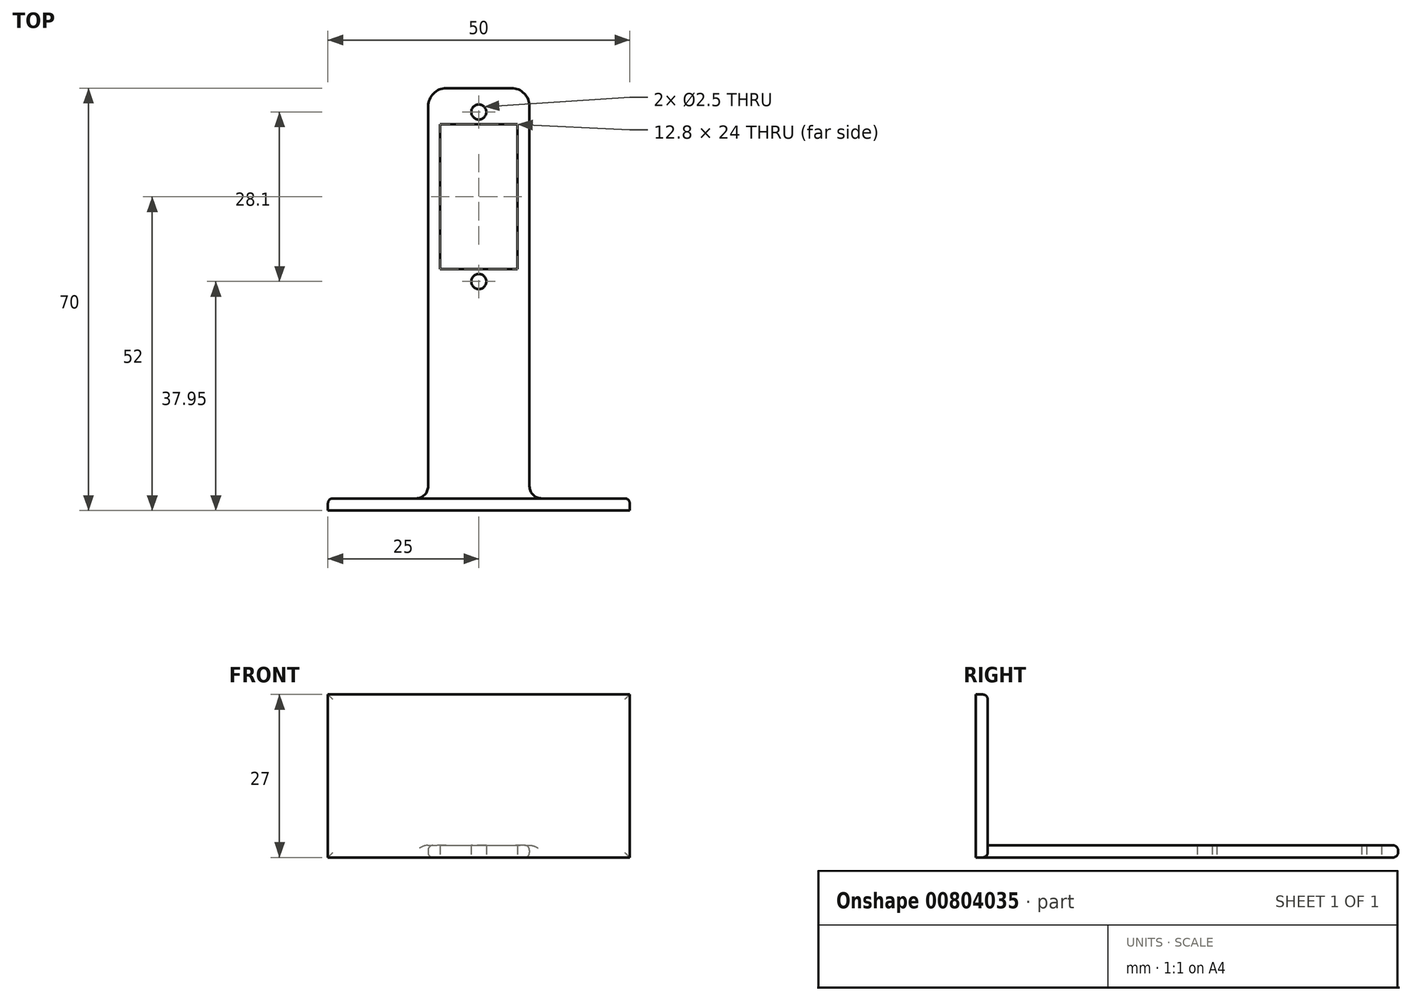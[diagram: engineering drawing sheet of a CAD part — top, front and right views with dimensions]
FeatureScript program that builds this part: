
annotation { "Feature Type Name" : "Feature", "Feature Type Description" : "" }
export const myFeature = defineFeature(function(context is Context, id is Id, definition is map)
    precondition{}
    {
        {
            assignVariable(context, id + "F0", {"name" : "wallT", "anyValue" : 2});
        }
        {
            var Q0;
            Q0=qCreatedBy(makeId("Top.planeOp"),FACE);
            var sketch = newSketch(context, id + "F1", { "sketchPlane" : qUnion([Q0])});
            skLineSegment(sketch, "E0.bottom", {"start": v(-5.4, 35) * mm, "end": v(5.4, 35) * mm});
            skLineSegment(sketch, "E0.top", {"start": v(-8.4, -35) * mm, "end": v(8.4, -35) * mm});
            skLineSegment(sketch, "E0.left", {"start": v(-8.4, 32) * mm, "end": v(-8.4, -35) * mm});
            skLineSegment(sketch, "E0.right", {"start": v(8.4, 32) * mm, "end": v(8.4, -35) * mm});
            skLineSegment(sketch, "E1", {"start": v(-6.63, 0) * mm, "end": v(6.86, 0) * mm, "construction": true});
            skLineSegment(sketch, "E2", {"start": v(0, 7.52) * mm, "end": v(0, -9.29) * mm, "construction": true});
            skLineSegment(sketch, "E3.bottom", {"start": v(-6.4, 29) * mm, "end": v(6.4, 29) * mm});
            skLineSegment(sketch, "E3.top", {"start": v(-6.4, 5) * mm, "end": v(6.4, 5) * mm});
            skLineSegment(sketch, "E3.left", {"start": v(-6.4, 29) * mm, "end": v(-6.4, 5) * mm});
            skLineSegment(sketch, "E3.right", {"start": v(6.4, 29) * mm, "end": v(6.4, 5) * mm});
            skCircle(sketch, "E4", {"center": v(0, 31.05) * mm, "radius": 1.25 * mm});
            skCircle(sketch, "E5", {"center": v(0, 2.95) * mm, "radius": 1.25 * mm});
            skLineSegment(sketch, "E6", {"start": v(-7.84, 17) * mm, "end": v(7.5, 17) * mm, "construction": true});
            skPoint(sketch, "E6.startSnap0", {"position": v(-6.4, 17) * mm});
            skPoint(sketch, "E7.visualSharp", {"position": v(-8.4, 35) * mm});
            skArc(sketch, "E7.filletArc", {"start": v(-5.4, 35) * mm, "mid": v(-7.52, 34.12) * mm, "end": v(-8.4, 32) * mm});
            skPoint(sketch, "E8.visualSharp", {"position": v(8.4, 35) * mm});
            skArc(sketch, "E8.filletArc", {"start": v(8.4, 32) * mm, "mid": v(7.52, 34.12) * mm, "end": v(5.4, 35) * mm});
            skSolve(sketch);
        }
        {
            var Q0;
            Q0 = qSketchRegion(id + "F1", true);
            extrude(context, id + "F2", {"entities" : qUnion([Q0]), "depth" : (getVariable(context, 'wallT')) * mm, "offsetDistance" : 25 * mm});
        }
        {
            var Q0;
            Q0=makeQuery(id+"F2.opExtrude","CAP_FACE",FACE,{"disambiguationData":[OSD([sQuery(id+"F1.wireOp",EDGE,"E0.bottom"),sQuery(id+"F1.wireOp",EDGE,"E0.top"),sQuery(id+"F1.wireOp",EDGE,"E0.left"),sQuery(id+"F1.wireOp",EDGE,"E0.right")])],"isStart":false});
            var sketch = newSketch(context, id + "F3", { "sketchPlane" : qUnion([Q0])});
            skLineSegment(sketch, "E9.bottom", {"start": v(-8.4, -35) * mm, "end": v(8.4, -35) * mm});
            skLineSegment(sketch, "E9.top", {"start": v(-8.4, -33) * mm, "end": v(8.4, -33) * mm});
            skLineSegment(sketch, "E9.left", {"start": v(-8.4, -35) * mm, "end": v(-8.4, -33) * mm});
            skLineSegment(sketch, "E9.right", {"start": v(8.4, -35) * mm, "end": v(8.4, -33) * mm});
            skSolve(sketch);
        }
        {
            var Q0;
            Q0 = qSketchRegion(id + "F3", true);
            extrude(context, id + "F4", {"entities" : qUnion([Q0]), "operationType" : NewBodyOperationType.ADD, "depth" : 25 * mm, "offsetDistance" : 25 * mm});
        }
        {
            var Q0;
            Q0=makeQuery(id+"F4.boolean.opBoolean","MERGE",FACE,{"derivedFrom":[makeQuery(id+"F2.opExtrude","SWEPT_FACE",FACE,{"disambiguationData":[OSD([sQuery(id+"F1.wireOp",EDGE,"E0.top")])]}),makeQuery(id+"F4.opExtrude","SWEPT_FACE",FACE,{"disambiguationData":[OSD([sQuery(id+"F3.wireOp",EDGE,"E9.bottom")])]})]});
            var sketch = newSketch(context, id + "F5", { "sketchPlane" : qUnion([Q0])});
            skLineSegment(sketch, "E10.bottom", {"start": v(-25, 27) * mm, "end": v(25, 27) * mm});
            skLineSegment(sketch, "E10.top", {"start": v(-25, 0) * mm, "end": v(25, 0) * mm});
            skLineSegment(sketch, "E10.left", {"start": v(-25, 27) * mm, "end": v(-25, 0) * mm});
            skLineSegment(sketch, "E10.right", {"start": v(25, 27) * mm, "end": v(25, 0) * mm});
            skLineSegment(sketch, "E11", {"start": v(0, -3.84) * mm, "end": v(0, 7.26) * mm, "construction": true});
            skSolve(sketch);
        }
        {
            var Q0;
            Q0 = qSketchRegion(id + "F5", true);
            extrude(context, id + "F6", {"entities" : qUnion([Q0]), "operationType" : NewBodyOperationType.ADD, "oppositeDirection" : true, "depth" : (getVariable(context, 'wallT')) * mm, "offsetDistance" : 25 * mm});
        }
        {
            var Q0;
            Q0=makeQuery(id+"F6.boolean.opBoolean","INTERSECT",EDGE,{"derivedFrom":[makeQuery(id+"F4.boolean.opBoolean","MERGE",FACE,{"derivedFrom":[makeQuery(id+"F2.opExtrude","SWEPT_FACE",FACE,{"disambiguationData":[OSD([sQuery(id+"F1.wireOp",EDGE,"E0.left")])]}),makeQuery(id+"F4.opExtrude","SWEPT_FACE",FACE,{"disambiguationData":[OSD([sQuery(id+"F3.wireOp",EDGE,"E9.left")])]})]}),makeQuery(id+"F6.opExtrude","CAP_FACE",FACE,{"disambiguationData":[OSD([sQuery(id+"F5.wireOp",EDGE,"E10.bottom"),sQuery(id+"F5.wireOp",EDGE,"E10.top"),sQuery(id+"F5.wireOp",EDGE,"E10.left"),sQuery(id+"F5.wireOp",EDGE,"E10.right")])],"isStart":false})]});
            var Q1;
            Q1=makeQuery(id+"F4.opExtrude","CAP_EDGE",EDGE,{"disambiguationData":[OSD([sQuery(id+"F3.wireOp",EDGE,"E9.top")])],"isStart":true});
            var Q2;
            Q2=makeQuery(id+"F6.boolean.opBoolean","INTERSECT",EDGE,{"derivedFrom":[makeQuery(id+"F4.boolean.opBoolean","MERGE",FACE,{"derivedFrom":[makeQuery(id+"F2.opExtrude","SWEPT_FACE",FACE,{"disambiguationData":[OSD([sQuery(id+"F1.wireOp",EDGE,"E0.right")])]}),makeQuery(id+"F4.opExtrude","SWEPT_FACE",FACE,{"disambiguationData":[OSD([sQuery(id+"F3.wireOp",EDGE,"E9.right")])]})]}),makeQuery(id+"F6.opExtrude","CAP_FACE",FACE,{"disambiguationData":[OSD([sQuery(id+"F5.wireOp",EDGE,"E10.bottom"),sQuery(id+"F5.wireOp",EDGE,"E10.top"),sQuery(id+"F5.wireOp",EDGE,"E10.left"),sQuery(id+"F5.wireOp",EDGE,"E10.right")])],"isStart":false})]});
            fillet(context, id + "F7", {"entities" : qUnion([Q0, Q1, Q2]), "radius" : 2 * mm, "tangentPropagation" : true, "allowEdgeOverflow" : false});
        }
        {
            var Q0;
            Q0=makeQuery(id+"F4.boolean.opBoolean","MERGE",FACE,{"derivedFrom":[makeQuery(id+"F2.opExtrude","SWEPT_FACE",FACE,{"disambiguationData":[OSD([sQuery(id+"F1.wireOp",EDGE,"E0.left")])]}),makeQuery(id+"F4.opExtrude","SWEPT_FACE",FACE,{"disambiguationData":[OSD([sQuery(id+"F3.wireOp",EDGE,"E9.left")])]})]});
            var Q1;
            Q1=makeQuery(id+"F4.boolean.opBoolean","MERGE",FACE,{"derivedFrom":[makeQuery(id+"F2.opExtrude","SWEPT_FACE",FACE,{"disambiguationData":[OSD([sQuery(id+"F1.wireOp",EDGE,"E0.right")])]}),makeQuery(id+"F4.opExtrude","SWEPT_FACE",FACE,{"disambiguationData":[OSD([sQuery(id+"F3.wireOp",EDGE,"E9.right")])]})]});
            var Q2;
            Q2=makeQuery(id+"F2.opExtrude","SWEPT_FACE",FACE,{"disambiguationData":[OSD([sQuery(id+"F1.wireOp",EDGE,"E0.bottom")])]});
            var Q3;
            Q3=makeQuery(id+"F6.opExtrude","CAP_EDGE",EDGE,{"disambiguationData":[OSD([sQuery(id+"F5.wireOp",EDGE,"E10.right")])],"isStart":false});
            var Q4;
            Q4=makeQuery(id+"F6.boolean.opBoolean","MERGE",EDGE,{"derivedFrom":[makeQuery(id+"F4.opExtrude","CAP_EDGE",EDGE,{"disambiguationData":[OSD([sQuery(id+"F3.wireOp",EDGE,"E9.top")])],"isStart":false}),makeQuery(id+"F6.opExtrude","CAP_EDGE",EDGE,{"disambiguationData":[OSD([sQuery(id+"F5.wireOp",EDGE,"E10.bottom")])],"isStart":false})]});
            var Q5;
            Q5=makeQuery(id+"F6.opExtrude","CAP_EDGE",EDGE,{"disambiguationData":[OSD([sQuery(id+"F5.wireOp",EDGE,"E10.left")])],"isStart":false});
            fillet(context, id + "F8", {"entities" : qUnion([Q0, Q1, Q2, Q3, Q4, Q5]), "radius" : (getVariable(context, 'wallT') * .4) * mm, "tangentPropagation" : true, "allowEdgeOverflow" : false});
        }
    });
